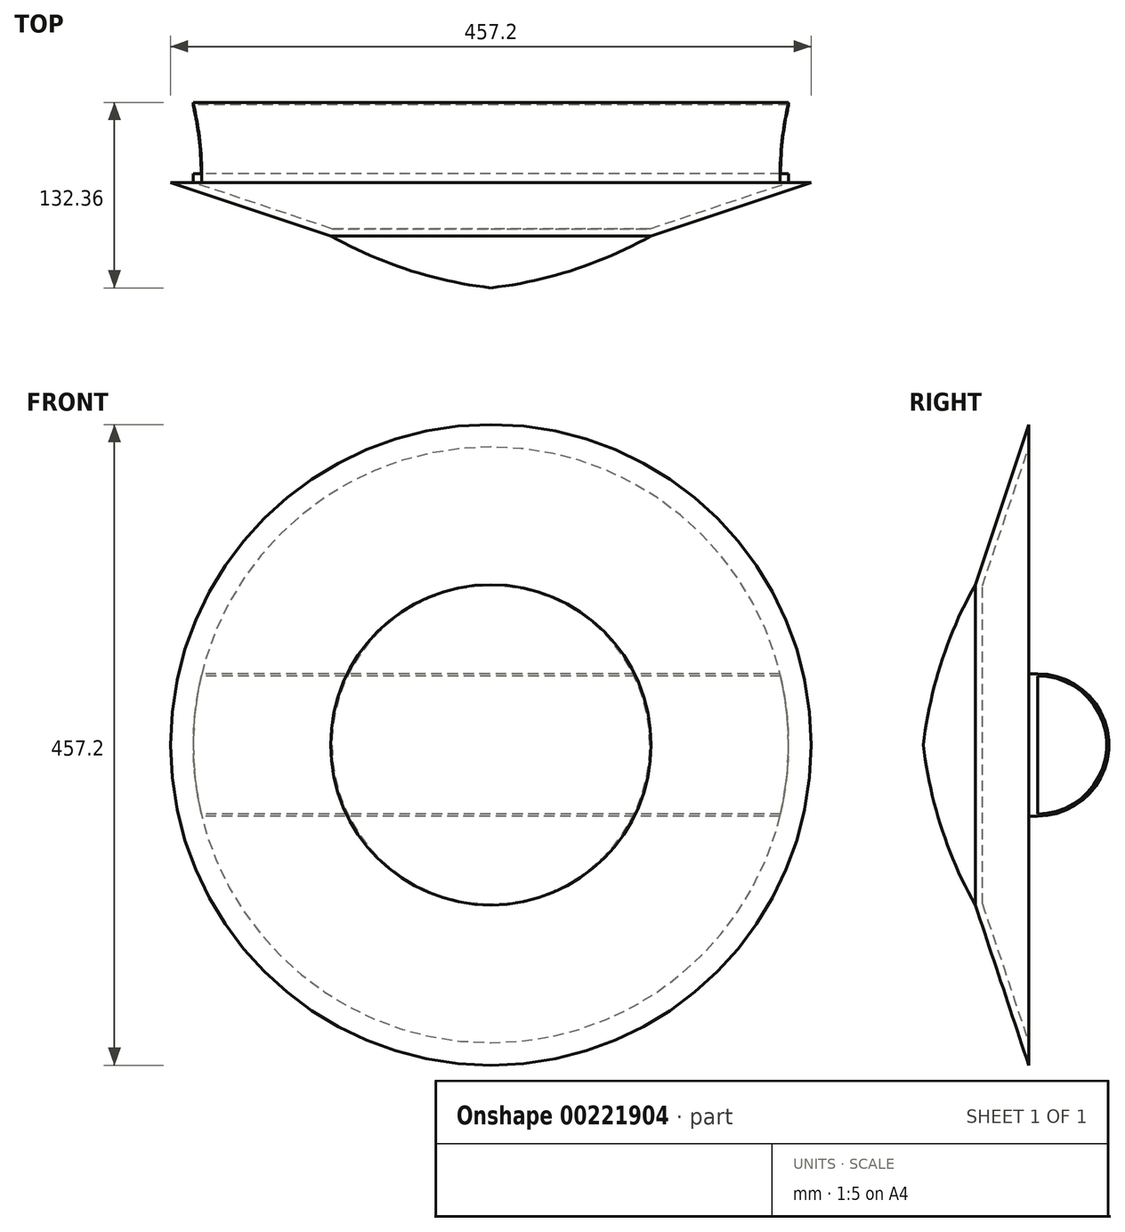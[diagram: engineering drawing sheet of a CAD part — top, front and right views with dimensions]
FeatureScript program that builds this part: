
annotation { "Feature Type Name" : "Feature", "Feature Type Description" : "" }
export const myFeature = defineFeature(function(context is Context, id is Id, definition is map)
    precondition{}
    {
        {
            var Q0;
            Q0=qCreatedBy(makeId("Front.planeOp"),FACE);
            var sketch = newSketch(context, id + "F0", { "sketchPlane" : qUnion([Q0])});
            skCircle(sketch, "E0", {"center": v(0, 0) * mm, "radius": 228.6 * mm});
            skSolve(sketch);
        }
        {
            var Q0;
            Q0=qCreatedBy(makeId("Front.planeOp"),FACE);
            cPlane(context, id + "F1", {"entities" : qUnion([Q0]), "cplaneType" : CPlaneType.OFFSET, "offset" : 38.1 * mm, "width" : 152.4 * mm, "height" : 152.4 * mm});
        }
        {
            var Q0;
            Q0=qCreatedBy(id+"F1.planeOp",FACE);
            var sketch = newSketch(context, id + "F2", { "sketchPlane" : qUnion([Q0])});
            skCircle(sketch, "E1", {"center": v(0, 0) * mm, "radius": 114.3 * mm});
            skSolve(sketch);
        }
        {
            var Q0;
            Q0=makeQuery(id+"F0.imprint","IMPRINT",FACE,{"disambiguationData":[TD([[makeQuery(id+"F0.imprint","IMPRINT",EDGE,{"derivedFrom":sQuery(id+"F0.wireOp",EDGE,"E0")}),1.0]])]});
            var Q1;
            Q1=makeQuery(id+"F2.imprint","IMPRINT",FACE,{"disambiguationData":[TD([[makeQuery(id+"F2.imprint","IMPRINT",EDGE,{"derivedFrom":sQuery(id+"F2.wireOp",EDGE,"E1")}),1.0]])]});
            loft(context, id + "F3", {"sheetProfilesArray" : [{ "sheetProfileEntities" : qUnion([Q0]) }, { "sheetProfileEntities" : qUnion([Q1]) }]});
        }
        {
            var Q0;
            Q0=makeQuery(id+"F3.opLoft","CAP_FACE",FACE,{"disambiguationData":[OSD([makeQuery(id+"F0.imprint","IMPRINT",FACE,{"disambiguationData":[TD([[makeQuery(id+"F0.imprint","IMPRINT",EDGE,{"derivedFrom":sQuery(id+"F0.wireOp",EDGE,"E0")}),1.0]])]})])],"isStart":true});
            shell(context, id + "F4", {"entities" : qUnion([Q0]), "thickness" : 5.08 * mm});
        }
        {
            var Q0;
            Q0=qCreatedBy(makeId("Right.planeOp"),FACE);
            var sketch = newSketch(context, id + "F5", { "sketchPlane" : qUnion([Q0])});
            skLineSegment(sketch, "E2", {"start": v(-38.1, 0) * mm, "end": v(-38.1, -114.3) * mm});
            skArc(sketch, "E3", {"start": v(-75.21, 0) * mm, "mid": v(-62.35, -59) * mm, "end": v(-38.1, -114.3) * mm});
            skLineSegment(sketch, "E4", {"start": v(-75.21, 0) * mm, "end": v(-38.1, 0) * mm});
            skSolve(sketch);
        }
        {
            var Q0;
            Q0=makeQuery(id+"F5.imprint","IMPRINT",FACE,{"disambiguationData":[TD([[makeQuery(id+"F5.imprint","IMPRINT",EDGE,{"derivedFrom":sQuery(id+"F5.wireOp",EDGE,"E2")}),-1.0]])]});
            var Q1;
            Q1=sQuery(id+"F5.wireOp",EDGE,"E4");
            revolve(context, id + "F6", {"operationType" : NewBodyOperationType.ADD, "entities" : qUnion([Q0]), "axis" : qUnion([Q1]), "revolveType" : RevolveType.FULL});
        }
        {
            var Q0;
            Q0=makeQuery(id+"F3.opLoft","CAP_FACE",FACE,{"disambiguationData":[OSD([makeQuery(id+"F0.imprint","IMPRINT",FACE,{"disambiguationData":[TD([[makeQuery(id+"F0.imprint","IMPRINT",EDGE,{"derivedFrom":sQuery(id+"F0.wireOp",EDGE,"E0")}),1.0]])]})])],"isStart":true});
            var sketch = newSketch(context, id + "F7", { "sketchPlane" : qUnion([Q0])});
            skLineSegment(sketch, "E5", {"start": v(-206.38, 50.8) * mm, "end": v(206.38, 50.8) * mm});
            skLineSegment(sketch, "E6", {"start": v(-206.38, -50.8) * mm, "end": v(206.38, -50.8) * mm});
            skLineSegment(sketch, "E7", {"start": v(-206.38, 0) * mm, "end": v(212.54, 0) * mm, "construction": true});
            skArc(sketch, "E8.0", {"start": v(206.38, 50.8) * mm, "mid": v(212.54, 0) * mm, "end": v(206.38, -50.8) * mm});
            skArc(sketch, "E9.trimOffspring", {"start": v(-206.38, -50.8) * mm, "mid": v(-212.54, 0) * mm, "end": v(-206.38, 50.8) * mm});
            skSolve(sketch);
        }
        {
            var Q0;
            Q0 = qSketchRegion(id + "F7", true);
            extrude(context, id + "F8", {"entities" : qUnion([Q0]), "depth" : 6.35 * mm});
        }
        {
            var Q0;
            Q0=qCreatedBy(makeId("Right.planeOp"),FACE);
            var sketch = newSketch(context, id + "F9", { "sketchPlane" : qUnion([Q0])});
            skLineSegment(sketch, "E10.0", {"start": v(6.35, -50.8) * mm, "end": v(6.35, -49.21) * mm});
            skArc(sketch, "E11", {"start": v(6.35, -50.8) * mm, "mid": v(57.15, 0) * mm, "end": v(6.35, 50.8) * mm});
            skArc(sketch, "E12.0", {"start": v(6.35, -49.21) * mm, "mid": v(55.56, 0) * mm, "end": v(6.35, 49.21) * mm});
            skLineSegment(sketch, "E13.trimOffspring", {"start": v(6.35, 49.21) * mm, "end": v(6.35, 50.8) * mm});
            skSolve(sketch);
        }
        {
            var Q0;
            Q0 = qSketchRegion(id + "F9", true);
            var Q1;
            Q1=makeQuery(id+"F8.opExtrude","SWEPT_FACE",FACE,{"disambiguationData":[OSD([sQuery(id+"F7.wireOp",EDGE,"E9.trimOffspring")])]});
            var Q2;
            Q2=makeQuery(id+"F8.opExtrude","SWEPT_BODY",BODY,{"disambiguationData":[OSD([sQuery(id+"F7.wireOp",EDGE,"E5"),sQuery(id+"F7.wireOp",EDGE,"E6"),sQuery(id+"F7.wireOp",EDGE,"E8.0"),sQuery(id+"F7.wireOp",EDGE,"E9.trimOffspring")])]});
            var Q3;
            Q3=makeQuery(id+"F8.opExtrude","SWEPT_FACE",FACE,{"disambiguationData":[OSD([sQuery(id+"F7.wireOp",EDGE,"E8.0")])]});
            extrude(context, id + "F10", {"entities" : qUnion([Q0]), "operationType" : NewBodyOperationType.ADD, "endBound" : BoundingType.UP_TO_SURFACE, "endBoundEntityFace" : qUnion([Q1]), "endBoundEntityBody" : qUnion([Q2]), "depth" : 25.4 * mm, "hasSecondDirection" : true, "secondDirectionBound" : SecondDirectionBoundingType.UP_TO_SURFACE, "secondDirectionOppositeDirection" : true, "secondDirectionBoundEntityFace" : qUnion([Q3]), "secondDirectionDepth" : 25.4 * mm});
        }
    });
